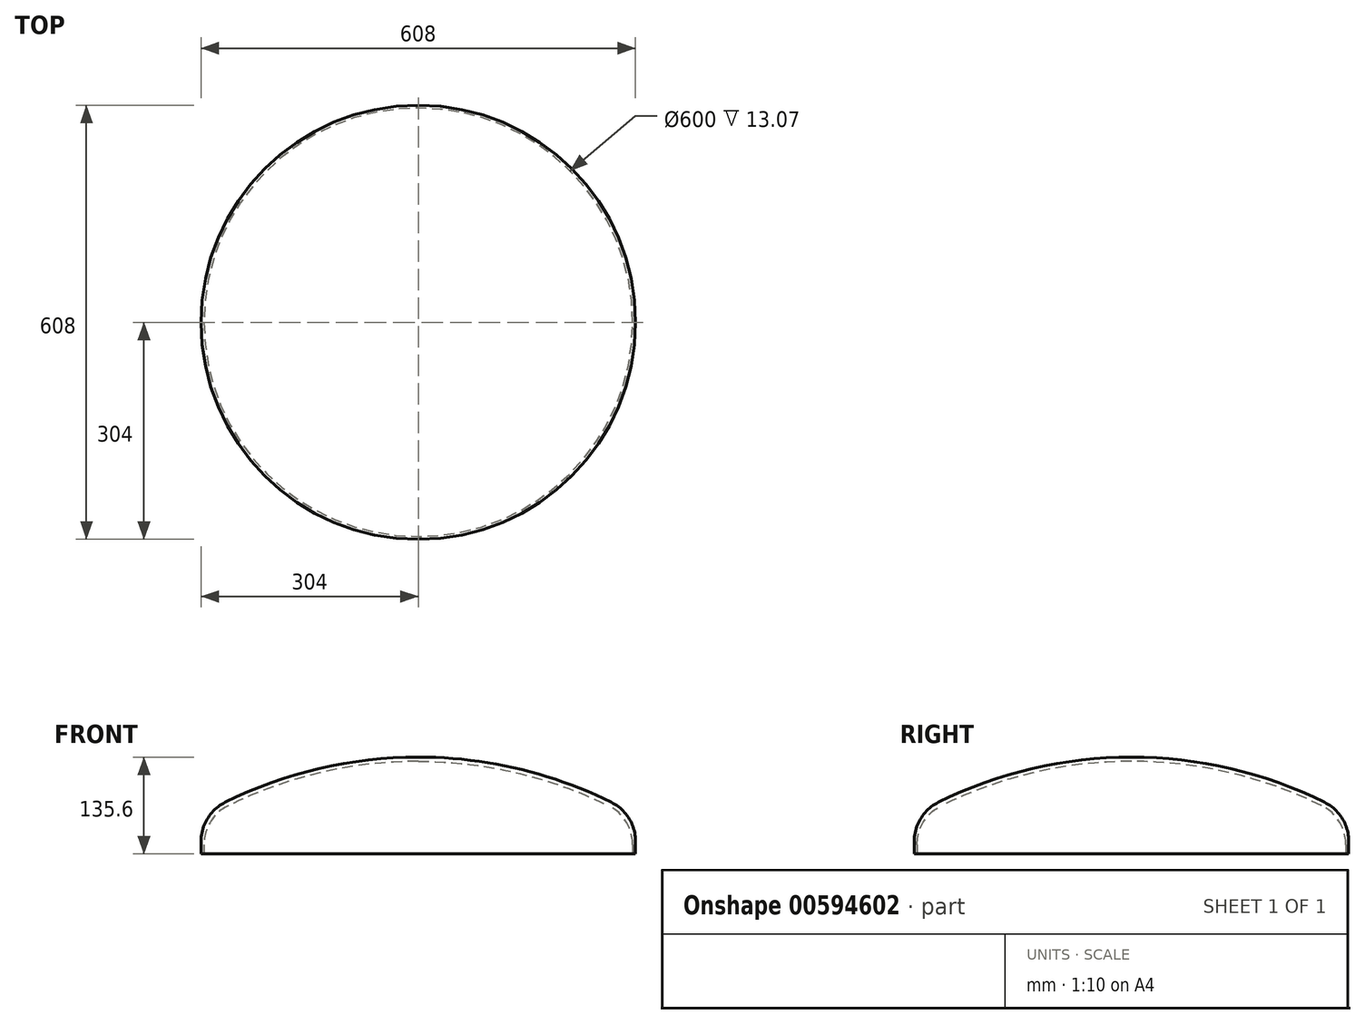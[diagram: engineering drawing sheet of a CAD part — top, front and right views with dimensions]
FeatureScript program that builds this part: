
annotation { "Feature Type Name" : "Feature", "Feature Type Description" : "" }
export const myFeature = defineFeature(function(context is Context, id is Id, definition is map)
    precondition{}
    {
        {
            var Q0;
            Q0=qCreatedBy(makeId("Front.planeOp"),FACE);
            var sketch = newSketch(context, id + "F0", { "sketchPlane" : qUnion([Q0])});
            skArc(sketch, "E0", {"start": v(-304, 519.6) * mm, "mid": v(0, -602) * mm, "end": v(304, 519.6) * mm});
            skLineSegment(sketch, "E1", {"start": v(0, 0) * mm, "end": v(721.01, 0) * mm});
            skLineSegment(sketch, "E2", {"start": v(304, 526.54) * mm, "end": v(304, 0) * mm});
            skCircle(sketch, "E3", {"center": v(0, 0) * mm, "radius": 608 * mm});
            skLineSegment(sketch, "E4", {"start": v(300, 521.92) * mm, "end": v(300, 0) * mm});
            skLineSegment(sketch, "E5", {"start": v(0, 0) * mm, "end": v(0, 190.02) * mm});
            skLineSegment(sketch, "E6.MirrorCS", {"start": v(600, 0) * mm, "end": v(600, 190.02) * mm});
            skLineSegment(sketch, "E7.MirrorCS", {"start": v(-300, 521.92) * mm, "end": v(-300, 0) * mm});
            skLineSegment(sketch, "E8.MirrorCS", {"start": v(-304, 526.54) * mm, "end": v(-304, 0) * mm});
            skLineSegment(sketch, "E9", {"start": v(300, 472.4) * mm, "end": v(304, 472.4) * mm});
            skArc(sketch, "E10.trimOffspring", {"start": v(300, 521.92) * mm, "mid": v(0, 602) * mm, "end": v(-300, 521.92) * mm});
            skLineSegment(sketch, "E11.trimOffspring", {"start": v(-304, 472.4) * mm, "end": v(-300, 472.4) * mm});
            skLineSegment(sketch, "E12", {"start": v(0, 0) * mm, "end": v(0, 678.68) * mm});
            skSolve(sketch);
        }
        {
            var Q0;
            {var subQ3=sQuery(id+"F0.wireOp",EDGE,"E9");Q0=makeQuery(id+"F0.imprint","IMPRINT",FACE,{"disambiguationData":[TD([[makeQuery(id+"F0.imprint","IMPRINT",EDGE,{"derivedFrom":subQ3}),1.0]])]});}
            var Q1;
            Q1=sQuery(id+"F0.wireOp",EDGE,"E12");
            revolve(context, id + "F1", {"entities" : qUnion([Q0]), "axis" : qUnion([Q1]), "revolveType" : RevolveType.FULL});
        }
        {
            var Q0;
            Q0=makeQuery(id+"F1.opRevolve","SWEPT_EDGE",EDGE,{"disambiguationData":[OSD([sQuery(id+"F0.wireOp",EDGE,"E4"),sQuery(id+"F0.wireOp",EDGE,"E10.trimOffspring")])]});
            fillet(context, id + "F2", {"entities" : qUnion([Q0]), "radius" : 60.8 * mm, "tangentPropagation" : true, "allowEdgeOverflow" : false});
        }
        {
            var Q0;
            Q0=makeQuery(id+"F1.opRevolve","SWEPT_EDGE",EDGE,{"disambiguationData":[OSD([sQuery(id+"F0.wireOp",EDGE,"E2"),sQuery(id+"F0.wireOp",EDGE,"E3")])]});
            fillet(context, id + "F3", {"entities" : qUnion([Q0]), "radius" : 60.8 * mm, "tangentPropagation" : true, "allowEdgeOverflow" : false});
        }
    });
